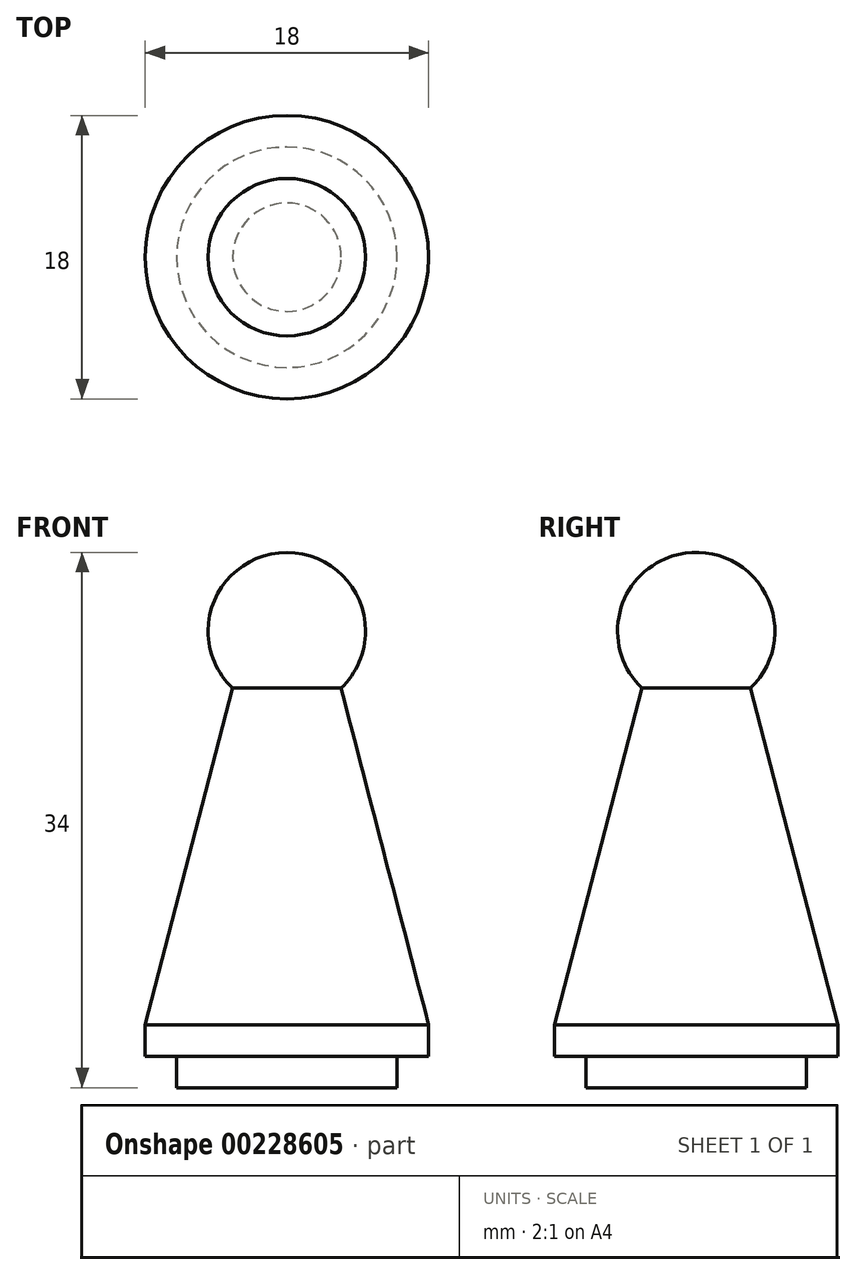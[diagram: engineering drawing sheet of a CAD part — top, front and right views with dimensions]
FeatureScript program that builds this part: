
annotation { "Feature Type Name" : "Feature", "Feature Type Description" : "" }
export const myFeature = defineFeature(function(context is Context, id is Id, definition is map)
    precondition{}
    {
        {
            var Q0;
            Q0=qCreatedBy(makeId("Top.planeOp"),FACE);
            var sketch = newSketch(context, id + "F0", { "sketchPlane" : qUnion([Q0])});
            skCircle(sketch, "E0", {"center": v(0, 0) * mm, "radius": 7 * mm});
            skSolve(sketch);
        }
        {
            var Q0;
            Q0=makeQuery(id+"F0.imprint","IMPRINT",FACE,{"disambiguationData":[TD([[makeQuery(id+"F0.imprint","IMPRINT",EDGE,{"derivedFrom":sQuery(id+"F0.wireOp",EDGE,"E0")}),1.0]])]});
            extrude(context, id + "F1", {"entities" : qUnion([Q0]), "depth" : 2 * mm});
        }
        {
            var Q0;
            Q0=makeQuery(id+"F1.opExtrude","CAP_FACE",FACE,{"disambiguationData":[OSD([sQuery(id+"F0.wireOp",EDGE,"E0")])],"isStart":false});
            var sketch = newSketch(context, id + "F2", { "sketchPlane" : qUnion([Q0])});
            skCircle(sketch, "E1", {"center": v(0, 0) * mm, "radius": 9 * mm});
            skSolve(sketch);
        }
        {
            var Q0;
            Q0 = qSketchRegion(id + "F2", true);
            extrude(context, id + "F3", {"entities" : qUnion([Q0]), "operationType" : NewBodyOperationType.ADD, "depth" : 2 * mm});
        }
        {
            var Q0;
            Q0=makeQuery(id+"F3.opExtrude","CAP_FACE",FACE,{"disambiguationData":[OSD([sQuery(id+"F2.wireOp",EDGE,"E1")])],"isStart":false});
            cPlane(context, id + "F4", {"entities" : qUnion([Q0]), "cplaneType" : CPlaneType.OFFSET, "offset" : 25 * mm, "width" : 150 * mm, "height" : 150 * mm});
        }
        {
            var Q0;
            Q0=qCreatedBy(id+"F4.planeOp",FACE);
            var sketch = newSketch(context, id + "F5", { "sketchPlane" : qUnion([Q0])});
            skCircle(sketch, "E2", {"center": v(0, 0) * mm, "radius": 2.5 * mm});
            skSolve(sketch);
        }
        {
            var Q1;
            Q1=makeQuery(id+"F3.opExtrude","CAP_FACE",FACE,{"disambiguationData":[OSD([sQuery(id+"F2.wireOp",EDGE,"E1")])],"isStart":false});
            var Q2;
            Q2=makeQuery(id+"F5.imprint","IMPRINT",FACE,{"disambiguationData":[TD([[makeQuery(id+"F5.imprint","IMPRINT",EDGE,{"derivedFrom":sQuery(id+"F5.wireOp",EDGE,"E2")}),1.0]])]});
            loft(context, id + "F6", {"operationType" : NewBodyOperationType.ADD, "sheetProfilesArray" : [{ "sheetProfileEntities" : qUnion([Q1]) }, { "sheetProfileEntities" : qUnion([Q2]) }]});
        }
        {
            var Q0;
            Q0=qCreatedBy(id+"F4.planeOp",FACE);
            var sketch = newSketch(context, id + "F7", { "sketchPlane" : qUnion([Q0])});
            skArc(sketch, "E3", {"start": v(-5, 0) * mm, "mid": v(0, -5) * mm, "end": v(5, 0) * mm});
            skLineSegment(sketch, "E4", {"start": v(-5, 0) * mm, "end": v(5, 0) * mm});
            skSolve(sketch);
        }
        {
            var Q0;
            Q0 = qSketchRegion(id + "F7", true);
            var Q1;
            Q1=sQuery(id+"F7.wireOp",EDGE,"E4");
            revolve(context, id + "F8", {"operationType" : NewBodyOperationType.ADD, "entities" : qUnion([Q0]), "axis" : qUnion([Q1]), "revolveType" : RevolveType.FULL});
        }
    });
